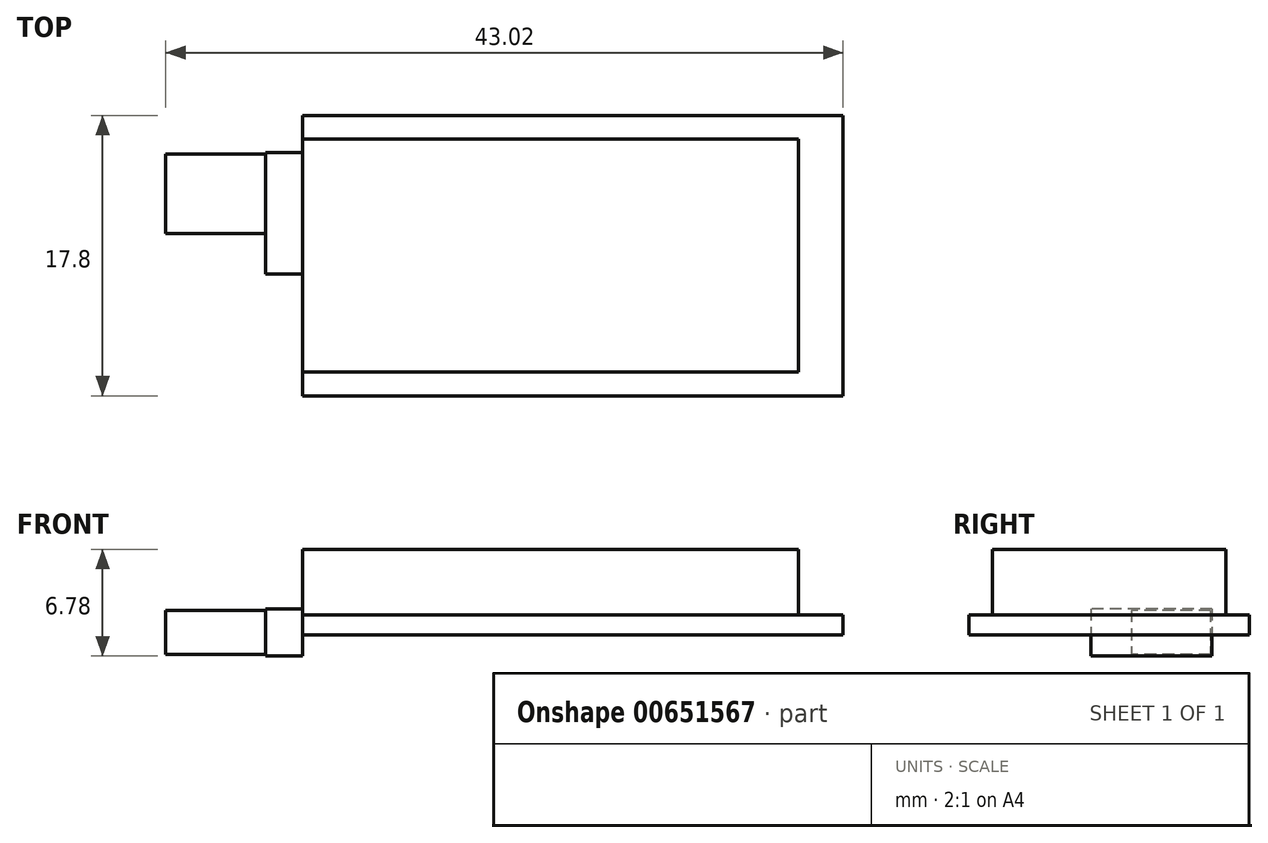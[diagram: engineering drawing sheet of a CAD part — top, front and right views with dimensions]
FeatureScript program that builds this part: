
annotation { "Feature Type Name" : "Feature", "Feature Type Description" : "" }
export const myFeature = defineFeature(function(context is Context, id is Id, definition is map)
    precondition{}
    {
        {
            var Q0;
            Q0=qCreatedBy(makeId("Top.planeOp"),FACE);
            var sketch = newSketch(context, id + "F0", { "sketchPlane" : qUnion([Q0])});
            skLineSegment(sketch, "E0.bottom", {"start": v(0, 0) * mm, "end": v(34.33, 0) * mm});
            skLineSegment(sketch, "E0.top", {"start": v(0, 17.8) * mm, "end": v(34.33, 17.8) * mm});
            skLineSegment(sketch, "E0.left", {"start": v(0, 0) * mm, "end": v(0, 17.8) * mm});
            skLineSegment(sketch, "E0.right", {"start": v(34.33, 0) * mm, "end": v(34.33, 17.8) * mm});
            skSolve(sketch);
        }
        {
            var Q0;
            Q0 = qSketchRegion(id + "F0", true);
            extrude(context, id + "F1", {"entities" : qUnion([Q0]), "depth" : 1.25 * mm, "offsetDistance" : 25 * mm});
        }
        {
            var Q0;
            Q0=makeQuery(id+"F1.opExtrude","CAP_FACE",FACE,{"disambiguationData":[OSD([sQuery(id+"F0.wireOp",EDGE,"E0.bottom"),sQuery(id+"F0.wireOp",EDGE,"E0.top"),sQuery(id+"F0.wireOp",EDGE,"E0.left"),sQuery(id+"F0.wireOp",EDGE,"E0.right")])],"isStart":false});
            var sketch = newSketch(context, id + "F2", { "sketchPlane" : qUnion([Q0])});
            skLineSegment(sketch, "E1.bottom", {"start": v(0, 16.3) * mm, "end": v(31.5, 16.3) * mm});
            skLineSegment(sketch, "E1.top", {"start": v(0, 1.5) * mm, "end": v(31.5, 1.5) * mm});
            skLineSegment(sketch, "E1.left", {"start": v(0, 16.3) * mm, "end": v(0, 1.5) * mm});
            skLineSegment(sketch, "E1.right", {"start": v(31.5, 16.3) * mm, "end": v(31.5, 1.5) * mm});
            skLineSegment(sketch, "E2", {"start": v(0, 17.8) * mm, "end": v(0, 16.3) * mm, "construction": true});
            skLineSegment(sketch, "E3", {"start": v(0, 0) * mm, "end": v(0, 1.5) * mm, "construction": true});
            skSolve(sketch);
        }
        {
            var Q0;
            Q0 = qSketchRegion(id + "F2", true);
            extrude(context, id + "F3", {"entities" : qUnion([Q0]), "operationType" : NewBodyOperationType.ADD, "depth" : 4.18 * mm, "offsetDistance" : 25 * mm});
        }
        {
            var Q0;
            Q0=makeQuery(id+"F3.boolean.opBoolean","MERGE",FACE,{"derivedFrom":[makeQuery(id+"F1.opExtrude","SWEPT_FACE",FACE,{"disambiguationData":[OSD([sQuery(id+"F0.wireOp",EDGE,"E0.left")])]}),makeQuery(id+"F3.opExtrude","SWEPT_FACE",FACE,{"disambiguationData":[OSD([sQuery(id+"F2.wireOp",EDGE,"E1.left")])]})]});
            var sketch = newSketch(context, id + "F4", { "sketchPlane" : qUnion([Q0])});
            skLineSegment(sketch, "E4.bottom", {"start": v(-15.44, 1.65) * mm, "end": v(-7.74, 1.65) * mm});
            skLineSegment(sketch, "E4.top", {"start": v(-15.44, -1.35) * mm, "end": v(-7.74, -1.35) * mm});
            skLineSegment(sketch, "E4.left", {"start": v(-15.44, 1.65) * mm, "end": v(-15.44, -1.35) * mm});
            skLineSegment(sketch, "E4.right", {"start": v(-7.74, 1.65) * mm, "end": v(-7.74, -1.35) * mm});
            skSolve(sketch);
        }
        {
            var Q0;
            Q0 = qSketchRegion(id + "F4", true);
            extrude(context, id + "F5", {"entities" : qUnion([Q0]), "operationType" : NewBodyOperationType.ADD, "depth" : 2.36 * mm, "offsetDistance" : 25 * mm});
        }
        {
            var Q0;
            Q0=makeQuery(id+"F5.opExtrude","CAP_FACE",FACE,{"disambiguationData":[OSD([sQuery(id+"F4.wireOp",EDGE,"E4.bottom"),sQuery(id+"F4.wireOp",EDGE,"E4.top"),sQuery(id+"F4.wireOp",EDGE,"E4.left"),sQuery(id+"F4.wireOp",EDGE,"E4.right")])],"isStart":false});
            var sketch = newSketch(context, id + "F6", { "sketchPlane" : qUnion([Q0])});
            skLineSegment(sketch, "E5.bottom", {"start": v(-15.34, 1.55) * mm, "end": v(-10.3, 1.55) * mm});
            skLineSegment(sketch, "E5.top", {"start": v(-15.34, -1.25) * mm, "end": v(-10.3, -1.25) * mm});
            skLineSegment(sketch, "E5.left", {"start": v(-15.34, 1.55) * mm, "end": v(-15.34, -1.25) * mm});
            skLineSegment(sketch, "E5.right", {"start": v(-10.3, 1.55) * mm, "end": v(-10.3, -1.25) * mm});
            skLineSegment(sketch, "E6", {"start": v(-15.44, 1.78) * mm, "end": v(-12.87, 1.78) * mm, "construction": true});
            skLineSegment(sketch, "E7", {"start": v(-12.87, 1.78) * mm, "end": v(-10.3, 1.78) * mm, "construction": true});
            skLineSegment(sketch, "E8", {"start": v(-10.3, 1.78) * mm, "end": v(-7.74, 1.78) * mm, "construction": true});
            skLineSegment(sketch, "E9", {"start": v(-15.34, 1.55) * mm, "end": v(-15.34, 1.65) * mm, "construction": true});
            skLineSegment(sketch, "E10", {"start": v(-15.34, 1.55) * mm, "end": v(-15.44, 1.55) * mm, "construction": true});
            skLineSegment(sketch, "E11", {"start": v(-15.34, -1.25) * mm, "end": v(-15.34, -1.35) * mm, "construction": true});
            skSolve(sketch);
        }
        {
            var Q0;
            Q0 = qSketchRegion(id + "F6", true);
            extrude(context, id + "F7", {"entities" : qUnion([Q0]), "operationType" : NewBodyOperationType.ADD, "depth" : 6.33 * mm, "offsetDistance" : 25 * mm});
        }
    });
